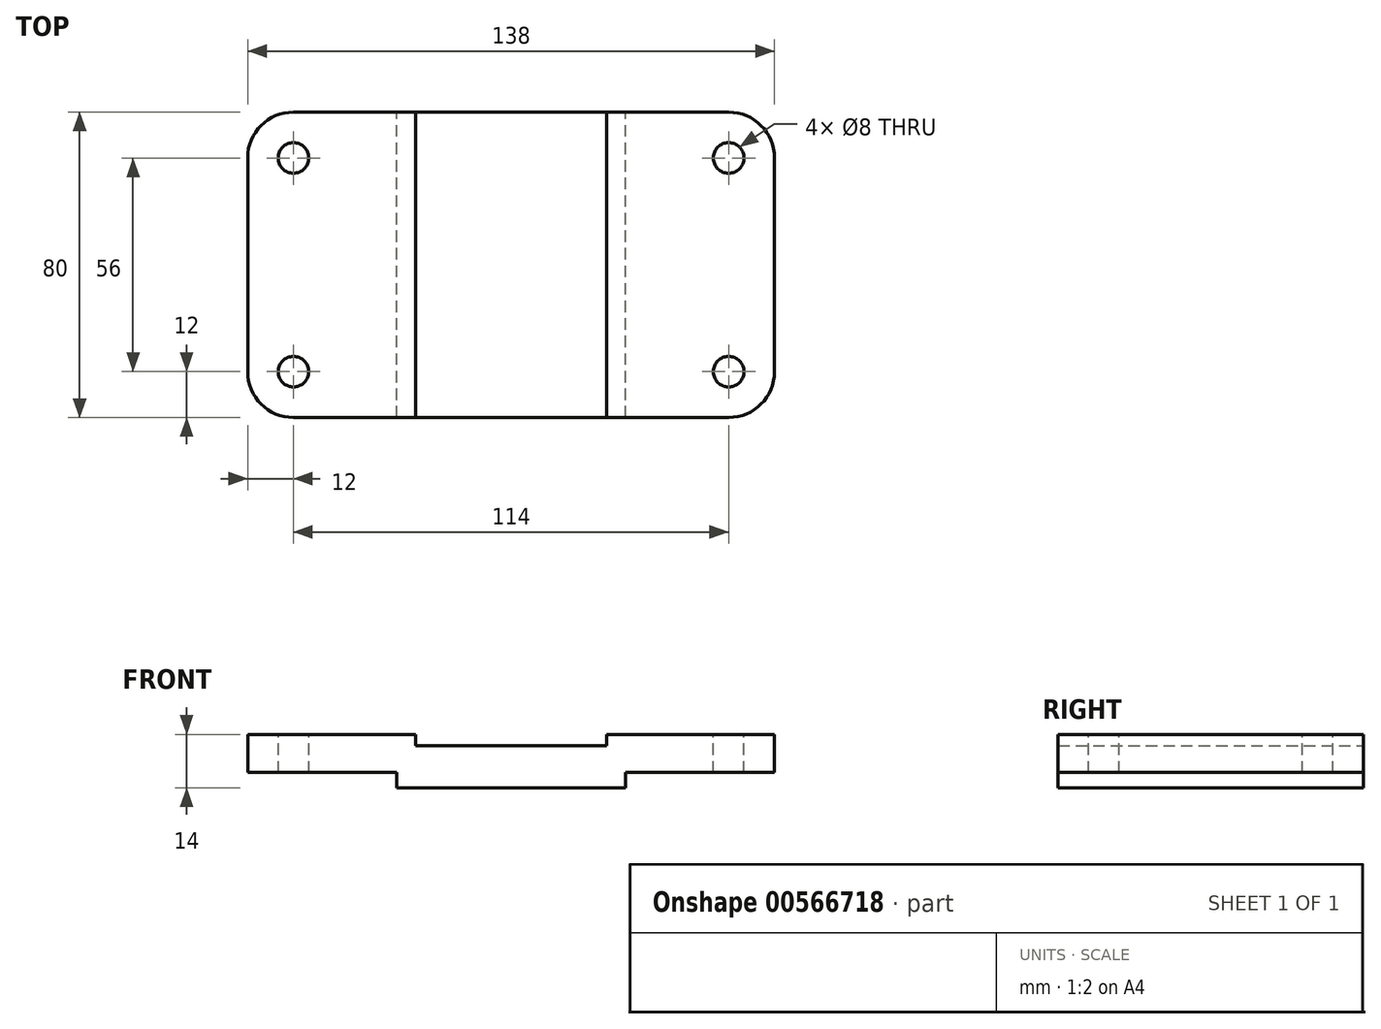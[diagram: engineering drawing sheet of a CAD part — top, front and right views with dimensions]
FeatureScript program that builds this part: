
annotation { "Feature Type Name" : "Feature", "Feature Type Description" : "" }
export const myFeature = defineFeature(function(context is Context, id is Id, definition is map)
    precondition{}
    {
        {
            var Q0;
            Q0=qCreatedBy(makeId("Front.planeOp"),FACE);
            var sketch = newSketch(context, id + "F0", { "sketchPlane" : qUnion([Q0])});
            skLineSegment(sketch, "E0.bottom", {"start": v(-69, -5) * mm, "end": v(-30, -5) * mm});
            skLineSegment(sketch, "E0.top", {"start": v(-69, 5) * mm, "end": v(-25, 5) * mm});
            skLineSegment(sketch, "E0.left", {"start": v(-69, -5) * mm, "end": v(-69, 5) * mm});
            skLineSegment(sketch, "E0.right", {"start": v(69, -5) * mm, "end": v(69, 5) * mm});
            skPoint(sketch, "E0.middle", {"position": v(0, 0) * mm});
            skLineSegment(sketch, "E1", {"start": v(-25, 5) * mm, "end": v(-25, 2) * mm});
            skLineSegment(sketch, "E2", {"start": v(-25, 2) * mm, "end": v(25, 2) * mm});
            skLineSegment(sketch, "E3", {"start": v(25, 2) * mm, "end": v(25, 5) * mm});
            skLineSegment(sketch, "E4.trimOffspring", {"start": v(25, 5) * mm, "end": v(69, 5) * mm});
            skLineSegment(sketch, "E5", {"start": v(-30, -5) * mm, "end": v(-30, -9) * mm});
            skLineSegment(sketch, "E6", {"start": v(-30, -9) * mm, "end": v(30, -9) * mm});
            skLineSegment(sketch, "E7", {"start": v(30, -9) * mm, "end": v(30, -5) * mm});
            skLineSegment(sketch, "E8.trimOffspring", {"start": v(30, -5) * mm, "end": v(69, -5) * mm});
            skLineSegment(sketch, "E9", {"start": v(0, 34.81) * mm, "end": v(0, -44.75) * mm, "construction": true});
            skSolve(sketch);
        }
        {
            var Q0;
            Q0 = qSketchRegion(id + "F0", true);
            extrude(context, id + "F1", {"entities" : qUnion([Q0]), "endBound" : BoundingType.SYMMETRIC, "depth" : 80 * mm, "offsetDistance" : 25 * mm});
        }
        {
            var Q0;
            Q0=qCreatedBy(makeId("Top.planeOp"),FACE);
            var sketch = newSketch(context, id + "F2", { "sketchPlane" : qUnion([Q0])});
            skPoint(sketch, "E10.visualSharp", {"position": v(-69, 40) * mm});
            skArc(sketch, "E10.filletArc", {"start": v(-57, 40) * mm, "mid": v(-65.49, 36.49) * mm, "end": v(-69, 28) * mm});
            skPoint(sketch, "E11.visualSharp", {"position": v(-69, -40) * mm});
            skArc(sketch, "E11.filletArc", {"start": v(-69, -28) * mm, "mid": v(-65.49, -36.49) * mm, "end": v(-57, -40) * mm});
            skPoint(sketch, "E12.visualSharp", {"position": v(69, -40) * mm});
            skArc(sketch, "E12.filletArc", {"start": v(57, -40) * mm, "mid": v(65.49, -36.49) * mm, "end": v(69, -28) * mm});
            skPoint(sketch, "E13.visualSharp", {"position": v(69, 40) * mm});
            skArc(sketch, "E13.filletArc", {"start": v(69, 28) * mm, "mid": v(65.49, 36.49) * mm, "end": v(57, 40) * mm});
            skCircle(sketch, "E14", {"center": v(-57, 28) * mm, "radius": 4 * mm});
            skCircle(sketch, "E15", {"center": v(57, 28) * mm, "radius": 4 * mm});
            skCircle(sketch, "E16", {"center": v(57, -28) * mm, "radius": 4 * mm});
            skCircle(sketch, "E17", {"center": v(-57, -28) * mm, "radius": 4 * mm});
            skPoint(sketch, "E18.0.3.end.orphan", {"position": v(-25, 40) * mm});
            skPoint(sketch, "E18.0.2.end.orphan", {"position": v(-25, -40) * mm});
            skPoint(sketch, "E19.0.0.end.orphan", {"position": v(25, 40) * mm});
            skPoint(sketch, "E19.0.2.start.orphan", {"position": v(25, -40) * mm});
            skLineSegment(sketch, "E20", {"start": v(-69, 28) * mm, "end": v(-69, 40) * mm});
            skLineSegment(sketch, "E21", {"start": v(57, 40) * mm, "end": v(69, 40) * mm});
            skLineSegment(sketch, "E22", {"start": v(69, -40) * mm, "end": v(69, -28) * mm});
            skLineSegment(sketch, "E23", {"start": v(57, -40) * mm, "end": v(69, -40) * mm});
            skLineSegment(sketch, "E24", {"start": v(-69, -28) * mm, "end": v(-69, -40) * mm});
            skLineSegment(sketch, "E25", {"start": v(-69, -40) * mm, "end": v(-57, -40) * mm});
            skLineSegment(sketch, "E26", {"start": v(69, 28) * mm, "end": v(69, 40) * mm});
            skLineSegment(sketch, "E27", {"start": v(-57, 40) * mm, "end": v(-69, 40) * mm});
            skSolve(sketch);
        }
        {
            var Q0;
            Q0 = qSketchRegion(id + "F2", true);
            extrude(context, id + "F3", {"entities" : qUnion([Q0]), "operationType" : NewBodyOperationType.REMOVE, "endBound" : BoundingType.SYMMETRIC, "oppositeDirection" : true, "depth" : 80 * mm, "offsetDistance" : 25 * mm});
        }
    });
